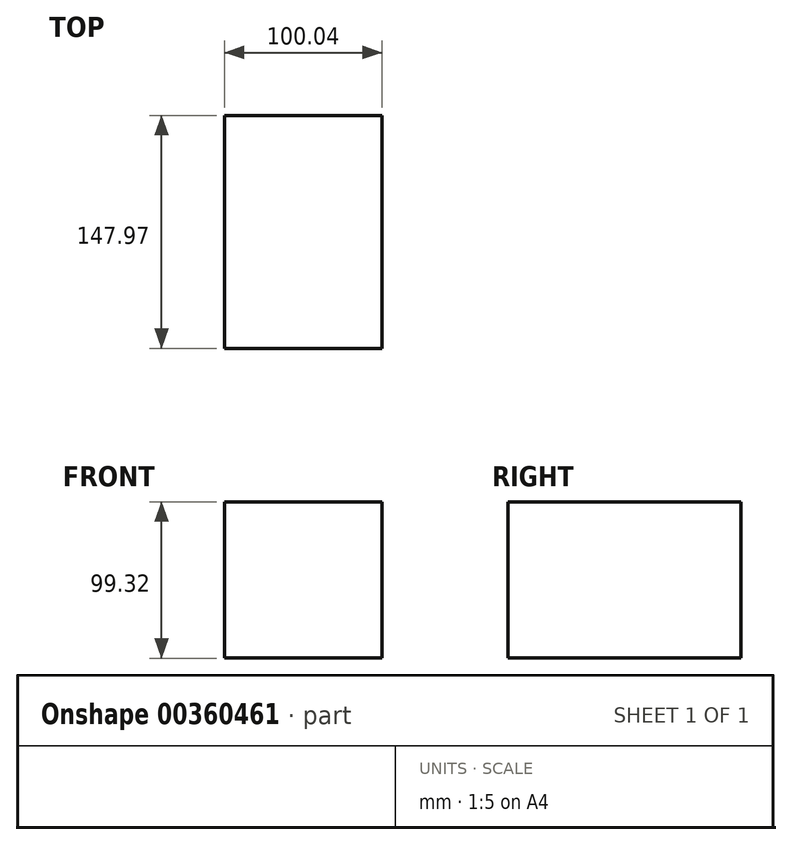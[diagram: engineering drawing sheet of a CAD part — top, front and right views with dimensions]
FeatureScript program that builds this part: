
annotation { "Feature Type Name" : "Feature", "Feature Type Description" : "" }
export const myFeature = defineFeature(function(context is Context, id is Id, definition is map)
    precondition{}
    {
        {
            var Q0;
            Q0=qCreatedBy(makeId("Front.planeOp"),FACE);
            var sketch = newSketch(context, id + "F0", { "sketchPlane" : qUnion([Q0])});
            skLineSegment(sketch, "E0.bottom", {"start": v(-30.61, 35.27) * mm, "end": v(69.43, 35.27) * mm});
            skLineSegment(sketch, "E0.top", {"start": v(-30.61, -64.05) * mm, "end": v(69.43, -64.05) * mm});
            skLineSegment(sketch, "E0.left", {"start": v(-30.61, 35.27) * mm, "end": v(-30.61, -64.05) * mm});
            skLineSegment(sketch, "E0.right", {"start": v(69.43, 35.27) * mm, "end": v(69.43, -64.05) * mm});
            skSolve(sketch);
        }
        {
            var Q0;
            Q0 = qSketchRegion(id + "F0", true);
            extrude(context, id + "F1", {"entities" : qUnion([Q0]), "depth" : 147.97 * mm});
        }
    });
